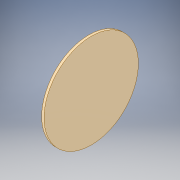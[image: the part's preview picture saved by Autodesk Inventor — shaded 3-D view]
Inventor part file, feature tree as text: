
AUTODESK INVENTOR PART (.ipt)
format: ipt  version: 2017 (Build 210142000, 142)  size: 93,184 bytes
history: native  units: in
note: dims shown in document units (in); Inventor stores cm internally (conversion verified against a paired STEP export)
features: sketch x2, extrude x2
ambient origin geometry x8: Origin, YZ Plane, XZ Plane, XY Plane, X Axis, Y Axis, Z Axis, Center Point
bodies: Solid1 (feature_tree)
feature tree (4):
  sketch  "Sketch1"  dims[d0=0.7874in d1=0.0394in d2=0.0in]
  extrude  "Extrusion1"  Depth=0.0394in TaperAngle=0.0deg
  extrude  "Extrusion2"  Depth=0.0394in TaperAngle=0.0deg
  sketch  "Sketch2"  dims[d3=1.5748in d4=0.0394in d5=0.0in]
